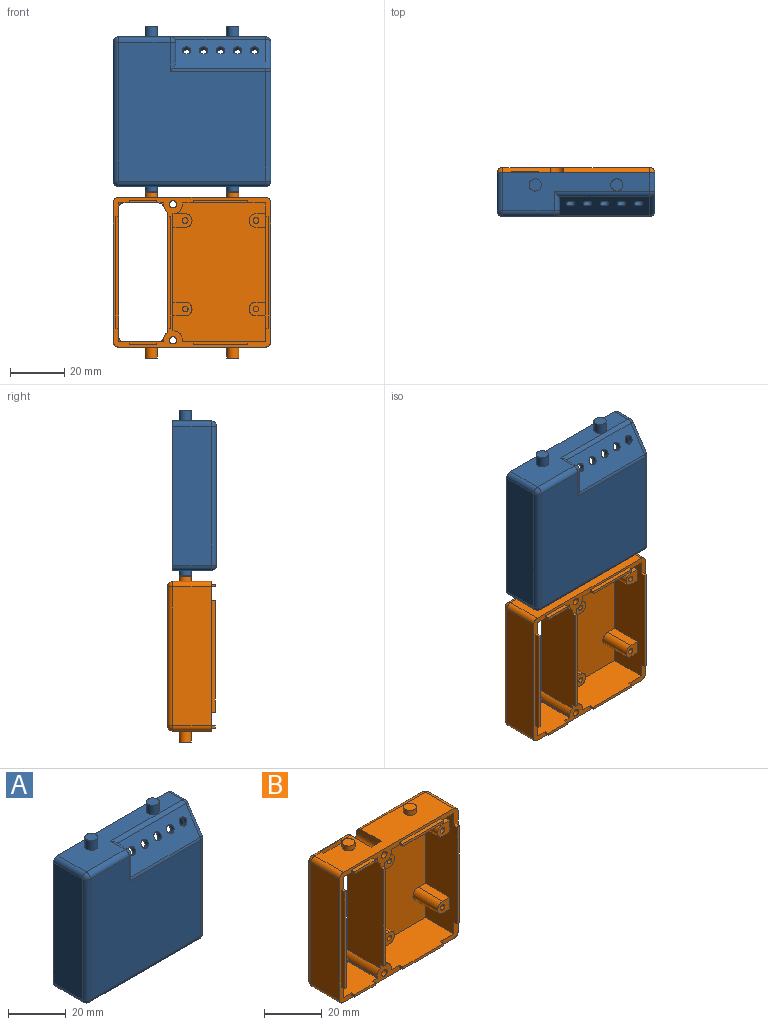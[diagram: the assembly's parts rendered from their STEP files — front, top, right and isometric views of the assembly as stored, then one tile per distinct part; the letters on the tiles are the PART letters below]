
ASSEMBLY  parts=2 mates=1
PART A: 117 faces, bbox 58x16x61 mm
  f0: plane 17x14mm, normal (0,0,1), area 216mm2, adj f2,f19,f27,f36,f97,f99,f100
  f1: plane 31x14mm, normal (0,0,1), area 392mm2, adj f2,f3,f16,f37,f105,f106,f108
  f2: plane 58x55mm, normal (0,1,0), area 343.2mm2, adj f0,f1,f3,f4,f17,f18,f20,f21
  f3: plane 51x14mm, normal (-1,0,0), area 509.9mm2, adj f1,f2,f5,f6,f7,f11,f15,f16
  f4: plane 45.53x14mm, normal (-1,0,0), area 555.4mm2, adj f2,f19,f34,f35,f82,f83,f84
  f5: plane 7.76x3.5mm, normal (0,0,1), area 27.2mm2, adj f3,f8,f15,f47
  f6: plane 8.5x3.5mm, normal (0,0,-1), area 29.8mm2, adj f3,f12,f16,f45
  f7: plane 8.5x3.5mm, normal (0,0,-1), area 29.8mm2, adj f3,f8,f16,f47
  f8: cylinder r=2.5mm len=8.5mm, axis (0,1,0), area 65.6mm2, adj f5,f7,f15,f16,f47
  f9: plane 8.5x4.5mm, normal (0,0,-1), area 38.2mm2, adj f10,f16,f39,f46
  f10: cylinder r=2.5mm len=8.5mm, axis (0,1,0), area 65.6mm2, adj f9,f15,f16,f42,f46
  f11: plane 8.5x3.5mm, normal (0,0,1), area 29.8mm2, adj f3,f12,f16,f45
  f12: cylinder r=2.5mm len=8.5mm, axis (0,1,0), area 66.8mm2, adj f6,f11,f16,f45
  f13: plane 8.5x4.5mm, normal (0,0,1), area 38.2mm2, adj f14,f16,f39,f44
  f14: cylinder r=2.5mm len=8.5mm, axis (0,1,0), area 66.8mm2, adj f13,f16,f43,f44
  f15: plane 34x10.61mm, normal (0,0.83,-0.55), area 368.4mm2, adj f3,f5,f8,f10,f16,f18,f28,f29
  f16: plane 40.39x34mm, normal (0,1,0), area 1257.6mm2, adj f1,f3,f6,f7,f8,f9,f10,f11
  f17: plane 17x14mm, normal (0,0,-1), area 216mm2, adj f2,f19,f27,f33,f102,f103,f104
  f18: plane 31x6.93mm, normal (0,0,-1), area 172.8mm2, adj f2,f3,f15,f41,f94,f95,f96
  f19: plane 51x18mm, normal (0,1,0), area 913.9mm2, adj f0,f4,f17,f27,f33,f34,f35,f36
  f20: plane 51x14mm, normal (1,0,0), area 676.5mm2, adj f2,f66,f67,f74,f75
  f21: plane 54x14mm, normal (0,0,1), area 476.7mm2, adj f2,f62,f65,f66,f69,f70,f113,f115
  f22: plane 54x51mm, normal (0,-1,0), area 2382.8mm2, adj f61,f68,f69,f75,f76,f78
  f23: plane 51x14mm, normal (-1,0,0), area 714mm2, adj f2,f60,f61,f62
  f24: plane 54x14mm, normal (0,0,-1), area 724.2mm2, adj f2,f60,f67,f68,f109,f111
  f25: plane 33.89x10.61mm, normal (0,-0.83,0.55), area 381.4mm2, adj f26,f28,f29,f30,f31,f32,f65,f70
  f26: plane 7x4.67mm, normal (1,0,0), area 16.3mm2, adj f25,f70,f76
  f27: plane 51x14mm, normal (1,0,0), area 632mm2, adj f0,f2,f17,f19,f85,f87,f88
  f28: cylinder r=1.6mm len=3.77mm, axis (0,-0.83,0.55), area 20.1mm2, adj f15,f25
  f29: cylinder r=1.6mm len=3.77mm, axis (0,-0.83,0.55), area 20.1mm2, adj f15,f25
  f30: cylinder r=1.6mm len=3.77mm, axis (0,-0.83,0.55), area 20.1mm2, adj f15,f25
  f31: cylinder r=1.6mm len=3.77mm, axis (0,-0.83,0.55), area 20.1mm2, adj f15,f25
  f32: cylinder r=1.6mm len=3.77mm, axis (0,-0.83,0.55), area 20.1mm2, adj f15,f25
  f33: plane 14x0.5mm, normal (-1,0,0), area 7mm2, adj f2,f17,f19,f34
  f34: cylinder r=3mm len=14mm, axis (0,1,0), area 35.3mm2, adj f2,f4,f19,f33
  f35: cylinder r=3mm len=14mm, axis (0,1,0), area 35.3mm2, adj f2,f4,f19,f36
  f36: plane 14x0.5mm, normal (-1,0,0), area 7mm2, adj f0,f2,f19,f35
  f37: plane 14x0.5mm, normal (1,0,0), area 7mm2, adj f1,f2,f16,f38
  f38: cylinder r=3mm len=14mm, axis (0,1,0), area 66mm2, adj f2,f16,f37,f39
  f39: plane 44x14mm, normal (1,0,0), area 514.6mm2, adj f2,f9,f13,f15,f16,f38,f40,f42
  f40: cylinder r=3mm len=9.26mm, axis (0,1,0), area 40.2mm2, adj f2,f15,f39,f41
  f41: plane 7.26x0.5mm, normal (1,0,0), area 3.5mm2, adj f2,f15,f18,f40
  f42: plane 7.76x4.5mm, normal (0,0,1), area 34.9mm2, adj f10,f15,f39,f46
  f43: plane 8.5x4.5mm, normal (0,0,-1), area 38.2mm2, adj f14,f16,f39,f44
  f44: plane 7x5mm, normal (0,1,0), area 28.9mm2, adj f13,f14,f39,f43,f49
  f45: plane 6x5mm, normal (0,1,0), area 23.9mm2, adj f3,f6,f11,f12,f51
  f46: plane 7x5mm, normal (0,1,0), area 28.9mm2, adj f9,f10,f39,f42,f53
  f47: plane 6x5mm, normal (0,1,0), area 23.9mm2, adj f3,f5,f7,f8,f55
  f48: plane 2.1x2.1mm, normal (0,1,0), area 3.5mm2, adj f49
  f49: cylinder r=1.05mm len=8.5mm, axis (0,1,0), area 56.1mm2, adj f44,f48
  f50: plane 2.1x2.1mm, normal (0,1,0), area 3.5mm2, adj f51
  f51: cylinder r=1.05mm len=8.5mm, axis (0,1,0), area 56.1mm2, adj f45,f50
  f52: plane 2.1x2.1mm, normal (0,1,0), area 3.5mm2, adj f53
  f53: cylinder r=1.05mm len=8.5mm, axis (0,1,0), area 56.1mm2, adj f46,f52
  f54: plane 2.1x2.1mm, normal (0,1,0), area 3.5mm2, adj f55
  f55: cylinder r=1.05mm len=8.5mm, axis (0,1,0), area 56.1mm2, adj f47,f54
  f56: cylinder r=1.05mm len=7mm, axis (0,1,0), area 46.2mm2, adj f2,f57
  f57: plane 2.1x2.1mm, normal (0,1,0), area 1.1mm2, adj f56,f58,f59
  f58: cylinder r=1mm len=2mm, axis (0,1,0), area 2.3mm2, adj f57,f59
  f59: plane 2x1.39mm, normal (0,0.83,-0.55), area 2.8mm2, adj f57,f58
  f60: cylinder r=2mm len=14mm, axis (0,-1,0), area 44mm2, adj f2,f23,f24,f63
  f61: cylinder r=2mm len=51mm, axis (0,0,1), area 160.2mm2, adj f22,f23,f63,f64
  f62: cylinder r=2mm len=14mm, axis (0,1,0), area 44mm2, adj f2,f21,f23,f64
  f63: sphere r=2mm, area 6.3mm2, adj f60,f61,f68
  f64: sphere r=2mm, area 6.3mm2, adj f61,f62,f69
  f65: cylinder r=2mm len=35mm, axis (-1,0,0), area 67mm2, adj f21,f25,f70,f71
  f66: cylinder r=2mm len=6.93mm, axis (0,-1,0), area 21.8mm2, adj f2,f20,f21,f71
  f67: cylinder r=2mm len=14mm, axis (0,1,0), area 44mm2, adj f2,f20,f24,f72
  f68: cylinder r=2mm len=54mm, axis (-1,0,0), area 169.6mm2, adj f22,f24,f63,f72
  f69: cylinder r=2mm len=19mm, axis (1,0,0), area 59.7mm2, adj f21,f22,f64,f73
  f70: cylinder r=2mm len=7.07mm, axis (0,1,0), area 18.1mm2, adj f21,f25,f26,f65,f73
  f71: sphere r=2mm, area 3.9mm2, adj f65,f66,f74
  f72: sphere r=2mm, area 6.3mm2, adj f67,f68,f75
  f73: sphere r=2mm, area 6.3mm2, adj f69,f70,f76
  f74: cylinder r=2mm len=11.72mm, axis (0,0.55,0.83), area 40mm2, adj f20,f25,f71,f77
  f75: cylinder r=2mm len=40.39mm, axis (0,0,-1), area 126.9mm2, adj f20,f22,f72,f77
  f76: cylinder r=2mm len=10.61mm, axis (0,0,1), area 28.2mm2, adj f22,f25,f26,f73,f78
  f77: sphere r=2mm, area 2.4mm2, adj f74,f75,f78
  f78: cylinder r=2mm len=35mm, axis (-1,0,0), area 40.5mm2, adj f22,f25,f76,f77
  f79: cylinder r=1.05mm len=14mm, axis (0,1,0), area 92.4mm2, adj f2,f80
  f80: plane 2.1x2.1mm, normal (0,1,0), area 3.5mm2, adj f79
  f81: plane 41x2mm, normal (-1,0,0), area 82mm2, adj f2,f82,f83,f84
  f82: plane 2x1.1mm, normal (0,0,1), area 2.2mm2, adj f2,f4,f81,f84
  f83: plane 2x1.1mm, normal (0,0,-1), area 2.2mm2, adj f2,f4,f81,f84
  f84: plane 41x1.1mm, normal (0,1,0), area 45.1mm2, adj f4,f81,f82,f83
  f85: plane 2x1.1mm, normal (0,0,1), area 2.2mm2, adj f2,f27,f86,f88
  f86: plane 41x2mm, normal (1,0,0), area 82mm2, adj f2,f85,f87,f88
  f87: plane 2x1.1mm, normal (0,0,-1), area 2.2mm2, adj f2,f27,f86,f88
  f88: plane 41x1.1mm, normal (0,1,0), area 45.1mm2, adj f27,f85,f86,f87
  f89: plane 41x2mm, normal (-1,0,0), area 82mm2, adj f2,f90,f91,f92
  f90: plane 2x1.1mm, normal (0,0,1), area 2.2mm2, adj f2,f3,f89,f92
  f91: plane 2x1.1mm, normal (0,0,-1), area 2.2mm2, adj f2,f3,f89,f92
  f92: plane 41x1.1mm, normal (0,1,0), area 45.1mm2, adj f3,f89,f90,f91
  f93: plane 21x2mm, normal (0,0,-1), area 42mm2, adj f2,f94,f95,f96
  f94: plane 2x1.1mm, normal (-1,0,0), area 2.2mm2, adj f2,f18,f93,f96
  f95: plane 2x1.1mm, normal (1,0,0), area 2.2mm2, adj f2,f18,f93,f96
  f96: plane 21x1.1mm, normal (0,1,0), area 23.1mm2, adj f18,f93,f94,f95
  f97: plane 2x1.1mm, normal (-1,0,0), area 2.2mm2, adj f0,f2,f98,f100
  f98: plane 11x2mm, normal (0,0,1), area 22mm2, adj f2,f97,f99,f100
  f99: plane 2x1.1mm, normal (1,0,0), area 2.2mm2, adj f0,f2,f98,f100
  f100: plane 11x1.1mm, normal (0,1,0), area 12.1mm2, adj f0,f97,f98,f99
  f101: plane 11x2mm, normal (0,0,-1), area 22mm2, adj f2,f102,f103,f104
  f102: plane 2x1.1mm, normal (-1,0,0), area 2.2mm2, adj f2,f17,f101,f104
  f103: plane 2x1.1mm, normal (1,0,0), area 2.2mm2, adj f2,f17,f101,f104
  f104: plane 11x1.1mm, normal (0,1,0), area 12.1mm2, adj f17,f101,f102,f103
  f105: plane 2x1.1mm, normal (1,0,0), area 2.2mm2, adj f1,f2,f107,f108
  f106: plane 2x1.1mm, normal (-1,0,0), area 2.2mm2, adj f1,f2,f107,f108
  f107: plane 21x2mm, normal (0,0,1), area 42mm2, adj f2,f105,f106,f108
  f108: plane 21x1.1mm, normal (0,1,0), area 23.1mm2, adj f1,f105,f106,f107
  f109: cylinder r=2.25mm len=4.5mm, axis (0,0,1), area 28.3mm2, adj f24,f110
  f110: plane 4.5x4.5mm, normal (0,0,-1), area 15.9mm2, adj f109
  f111: cylinder r=2.25mm len=4.5mm, axis (0,0,1), area 28.3mm2, adj f24,f112
  f112: plane 4.5x4.5mm, normal (0,0,-1), area 15.9mm2, adj f111
  f113: cylinder r=2.25mm len=4.5mm, axis (0,0,-1), area 56.5mm2, adj f21,f114
  f114: plane 4.5x4.5mm, normal (0,0,1), area 15.9mm2, adj f113
  f115: cylinder r=2.25mm len=4.5mm, axis (0,0,-1), area 56.5mm2, adj f21,f116
  f116: plane 4.5x4.5mm, normal (0,0,1), area 15.9mm2, adj f115
PART B: 125 faces, bbox 58x17.5x61 mm
  f0: plane 1.92x1.45mm, normal (0,-1,0), area 0.6mm2, adj f24,f41,f42,f114
  f1: plane 2x2mm, normal (0,-1,0), area 0.9mm2, adj f24,f33,f115
  f2: plane 2x2mm, normal (0,-1,0), area 0.9mm2, adj f26,f33,f116
  f3: plane 2x2mm, normal (0,1,0), area 0.9mm2, adj f61,f66,f115
  f4: plane 2x2mm, normal (0,1,0), area 0.9mm2, adj f8,f66,f116
  f5: plane 54x14mm, normal (0,0,1), area 663.2mm2, adj f7,f10,f57,f61,f62,f101,f102,f104
  f6: cylinder r=1.35mm len=4mm, axis (0,-1,0), area 33.9mm2, adj f10,f101
  f7: cylinder r=2mm len=31.5mm, axis (-1,0,0), area 99mm2, adj f5,f31,f58,f102
  f8: cylinder r=2mm len=17.5mm, axis (1,0,0), area 49.9mm2, adj f4,f26,f30,f31,f67,f98,f122,f123
  f9: cylinder r=1.35mm len=4mm, axis (0,-1,0), area 33.9mm2, adj f10,f97
  f10: plane 58x55mm, normal (0,-1,0), area 366.3mm2, adj f5,f6,f9,f22,f23,f24,f25,f26
  f11: cylinder r=2.5mm len=12mm, axis (0,-1,0), area 94.2mm2, adj f12,f21,f43,f54
  f12: plane 12x3.5mm, normal (0,0,-1), area 42mm2, adj f11,f21,f32,f54
  f13: cylinder r=2.5mm len=12mm, axis (0,-1,0), area 94.2mm2, adj f14,f21,f44,f51
  f14: plane 12x4.5mm, normal (0,0,-1), area 54mm2, adj f13,f21,f22,f51
  f15: cylinder r=2.5mm len=12mm, axis (0,-1,0), area 94.2mm2, adj f16,f17,f21,f48
  f16: plane 12x3.5mm, normal (0,0,1), area 42mm2, adj f15,f21,f32,f48
  f17: plane 12x3.5mm, normal (0,0,-1), area 42mm2, adj f15,f21,f32,f48
  f18: cylinder r=2.5mm len=12mm, axis (0,-1,0), area 94.2mm2, adj f19,f20,f21,f45
  f19: plane 12x4.5mm, normal (0,0,-1), area 54mm2, adj f18,f21,f22,f45
  f20: plane 12x4.5mm, normal (0,0,1), area 54mm2, adj f18,f21,f22,f45
  f21: plane 51x34mm, normal (0,-1,0), area 1592mm2, adj f11,f12,f13,f14,f15,f16,f17,f18
  f22: plane 43x14mm, normal (1,0,0), area 482mm2, adj f10,f14,f19,f20,f21,f35,f36,f45
  f23: plane 30.5x15.5mm, normal (0,0,-1), area 457mm2, adj f10,f21,f32,f34,f69,f71,f72
  f24: plane 17.5x16.5mm, normal (0,0,-1), area 255.4mm2, adj f0,f1,f10,f33,f42,f61,f89,f91
  f25: plane 30.5x15.5mm, normal (0,0,1), area 457mm2, adj f10,f21,f32,f37,f77,f79,f80
  f26: plane 17.5x16.5mm, normal (0,0,1), area 255.4mm2, adj f2,f8,f10,f27,f33,f38,f94,f95
  f27: plane 1.92x1.45mm, normal (0,-1,0), area 0.6mm2, adj f26,f38,f39,f113
  f28: plane 51x14mm, normal (1,0,0), area 714mm2, adj f10,f57,f59,f60
  f29: plane 51x14mm, normal (-1,0,0), area 714mm2, adj f10,f62,f66,f68
  f30: plane 54x14mm, normal (0,0,-1), area 663.2mm2, adj f8,f10,f59,f65,f68,f97,f98,f100
  f31: plane 51x39.29mm, normal (0,1,0), area 1820.1mm2, adj f7,f8,f39,f40,f41,f60,f61,f65
  f32: plane 51x15.5mm, normal (-1,0,0), area 655.5mm2, adj f10,f12,f16,f17,f21,f23,f25,f43
  f33: plane 51x17.5mm, normal (1,0,0), area 869.5mm2, adj f1,f2,f10,f24,f26,f66,f86,f87
  f34: plane 14x0.5mm, normal (1,0,0), area 7mm2, adj f10,f21,f23,f35
  f35: cylinder r=3.5mm len=14mm, axis (0,-1,0), area 77mm2, adj f10,f21,f22,f34,f44
  f36: cylinder r=3.5mm len=14mm, axis (0,-1,0), area 77mm2, adj f10,f21,f22,f37
  f37: plane 14x0.5mm, normal (1,0,0), area 7mm2, adj f10,f21,f25,f36
  f38: plane 14x0.5mm, normal (-1,0,0), area 7mm2, adj f10,f26,f27,f39
  f39: cylinder r=3.5mm len=16mm, axis (0,-1,0), area 52mm2, adj f10,f27,f31,f38,f40,f113
  f40: plane 44.26x17.5mm, normal (-1,0,0), area 769.6mm2, adj f10,f31,f39,f41,f81,f83,f84
  f41: cylinder r=3.5mm len=16mm, axis (0,-1,0), area 52mm2, adj f0,f10,f31,f40,f42,f114
  f42: plane 14x0.5mm, normal (-1,0,0), area 7mm2, adj f0,f10,f24,f41
  f43: plane 12x3.5mm, normal (0,0,1), area 42mm2, adj f11,f21,f32,f54
  f44: plane 12x4.5mm, normal (0,0,1), area 54mm2, adj f13,f21,f35,f51
  f45: plane 7x5mm, normal (0,-1,0), area 28.9mm2, adj f18,f19,f20,f22,f47
  f46: plane 2.1x2.1mm, normal (0,-1,0), area 3.5mm2, adj f47
  f47: cylinder r=1.05mm len=12mm, axis (0,-1,0), area 79.2mm2, adj f45,f46
  f48: plane 6x5mm, normal (0,-1,0), area 23.9mm2, adj f15,f16,f17,f32,f50
  f49: plane 2.1x2.1mm, normal (0,-1,0), area 3.5mm2, adj f50
  f50: cylinder r=1.05mm len=12mm, axis (0,-1,0), area 79.2mm2, adj f48,f49
  f51: plane 7x5mm, normal (0,-1,0), area 28.9mm2, adj f13,f14,f22,f44,f53
  f52: plane 2.1x2.1mm, normal (0,-1,0), area 3.5mm2, adj f53
  f53: cylinder r=1.05mm len=12mm, axis (0,-1,0), area 79.2mm2, adj f51,f52
  f54: plane 6x5mm, normal (0,-1,0), area 23.9mm2, adj f11,f12,f32,f43,f56
  f55: plane 2.1x2.1mm, normal (0,-1,0), area 3.5mm2, adj f56
  f56: cylinder r=1.05mm len=12mm, axis (0,-1,0), area 79.2mm2, adj f54,f55
  f57: cylinder r=2mm len=14mm, axis (0,-1,0), area 44mm2, adj f5,f10,f28,f58
  f58: sphere r=2mm, area 6.3mm2, adj f7,f57,f60
  f59: cylinder r=2mm len=14mm, axis (0,1,0), area 44mm2, adj f10,f28,f30,f63
  f60: cylinder r=2mm len=51mm, axis (0,0,1), area 160.2mm2, adj f28,f31,f58,f63
  f61: cylinder r=2mm len=17.5mm, axis (-1,0,0), area 49.9mm2, adj f3,f5,f24,f31,f64,f104,f117,f118
  f62: cylinder r=2mm len=14mm, axis (0,1,0), area 44mm2, adj f5,f10,f29,f64
  f63: sphere r=2mm, area 6.3mm2, adj f59,f60,f65
  f64: sphere r=2mm, area 6.3mm2, adj f61,f62,f66
  f65: cylinder r=2mm len=31.5mm, axis (1,0,0), area 99mm2, adj f30,f31,f63,f100
  f66: cylinder r=2mm len=51mm, axis (0,0,-1), area 160.2mm2, adj f3,f4,f29,f33,f64,f67
  f67: sphere r=2mm, area 6.3mm2, adj f8,f66,f68
  f68: cylinder r=2mm len=14mm, axis (0,-1,0), area 44mm2, adj f10,f29,f30,f67
  f69: plane 1.5x1mm, normal (1,0,0), area 1.5mm2, adj f10,f23,f70,f72
  f70: plane 20x1.5mm, normal (0,0,1), area 30mm2, adj f10,f69,f71,f72
  f71: plane 1.5x1mm, normal (-1,0,0), area 1.5mm2, adj f10,f23,f70,f72
  f72: plane 20x1mm, normal (0,-1,0), area 20mm2, adj f23,f69,f70,f71
  f73: plane 1.5x1mm, normal (0,0,-1), area 1.5mm2, adj f10,f32,f74,f76
  f74: plane 41x1.5mm, normal (1,0,0), area 61.5mm2, adj f10,f73,f75,f76
  f75: plane 1.5x1mm, normal (0,0,1), area 1.5mm2, adj f10,f32,f74,f76
  f76: plane 41x1mm, normal (0,-1,0), area 41mm2, adj f32,f73,f74,f75
  f77: plane 1.5x1mm, normal (-1,0,0), area 1.5mm2, adj f10,f25,f78,f80
  f78: plane 20x1.5mm, normal (0,0,-1), area 30mm2, adj f10,f77,f79,f80
  f79: plane 1.5x1mm, normal (1,0,0), area 1.5mm2, adj f10,f25,f78,f80
  f80: plane 20x1mm, normal (0,-1,0), area 20mm2, adj f25,f77,f78,f79
  f81: plane 1.5x1.1mm, normal (0,0,-1), area 1.6mm2, adj f10,f40,f82,f84
  f82: plane 41x1.5mm, normal (1,0,0), area 61.5mm2, adj f10,f81,f83,f84
  f83: plane 1.5x1.1mm, normal (0,0,1), area 1.6mm2, adj f10,f40,f82,f84
  f84: plane 41x1.1mm, normal (0,-1,0), area 45.1mm2, adj f40,f81,f82,f83
  f85: plane 41x1.5mm, normal (-1,0,0), area 61.5mm2, adj f10,f86,f87,f88
  f86: plane 1.5x1mm, normal (0,0,-1), area 1.5mm2, adj f10,f33,f85,f88
  f87: plane 1.5x1mm, normal (0,0,1), area 1.5mm2, adj f10,f33,f85,f88
  f88: plane 41x1mm, normal (0,-1,0), area 41mm2, adj f33,f85,f86,f87
  f89: plane 1.5x1mm, normal (1,0,0), area 1.5mm2, adj f10,f24,f90,f92
  f90: plane 10x1.5mm, normal (0,0,1), area 15mm2, adj f10,f89,f91,f92
  f91: plane 1.5x1mm, normal (-1,0,0), area 1.5mm2, adj f10,f24,f90,f92
  f92: plane 10x1mm, normal (0,-1,0), area 10mm2, adj f24,f89,f90,f91
  f93: plane 10x1.5mm, normal (0,0,-1), area 15mm2, adj f10,f94,f95,f96
  f94: plane 1.5x1mm, normal (1,0,0), area 1.5mm2, adj f10,f26,f93,f96
  f95: plane 1.5x1mm, normal (-1,0,0), area 1.5mm2, adj f10,f26,f93,f96
  f96: plane 10x1mm, normal (0,-1,0), area 10mm2, adj f26,f93,f94,f95
  f97: plane 5x5mm, normal (0,1,0), area 16.6mm2, adj f9,f30,f98,f99,f100
  f98: plane 12x2.5mm, normal (1,0,0), area 29.1mm2, adj f8,f30,f31,f97,f99
  f99: cylinder r=2.5mm len=12mm, axis (0,1,0), area 94.2mm2, adj f31,f97,f98,f100
  f100: plane 12x2.5mm, normal (-1,0,0), area 29.1mm2, adj f30,f31,f65,f97,f99
  f101: plane 5x5mm, normal (0,1,0), area 16.6mm2, adj f5,f6,f102,f103,f104
  f102: plane 12x2.5mm, normal (-1,0,0), area 29.1mm2, adj f5,f7,f31,f101,f103
  f103: cylinder r=2.5mm len=12mm, axis (0,1,0), area 94.2mm2, adj f31,f101,f102,f104
  f104: plane 12x2.5mm, normal (1,0,0), area 29.1mm2, adj f5,f31,f61,f101,f103
  f105: cylinder r=2.25mm len=4.5mm, axis (0,0,1), area 56.5mm2, adj f30,f106
  f106: plane 4.5x4.5mm, normal (0,0,-1), area 15.9mm2, adj f105
  f107: cylinder r=2.25mm len=4.5mm, axis (0,0,1), area 56.5mm2, adj f30,f108
  f108: plane 4.5x4.5mm, normal (0,0,-1), area 15.9mm2, adj f107
  f109: cylinder r=2.25mm len=4.5mm, axis (0,0,-1), area 28.3mm2, adj f5,f110
  f110: plane 4.5x4.5mm, normal (0,0,1), area 15.9mm2, adj f109
  f111: cylinder r=2.25mm len=4.5mm, axis (0,0,-1), area 28.3mm2, adj f5,f112
  f112: plane 4.5x4.5mm, normal (0,0,1), area 15.9mm2, adj f111
  f113: cylinder r=2mm len=2mm, axis (0,-1,0), area 5.2mm2, adj f26,f27,f31,f39
  f114: cylinder r=2mm len=2mm, axis (0,-1,0), area 5.2mm2, adj f0,f24,f31,f41
  f115: cylinder r=2mm len=2mm, axis (0,-1,0), area 6.3mm2, adj f1,f3,f24,f33
  f116: cylinder r=2mm len=2mm, axis (0,-1,0), area 6.3mm2, adj f2,f4,f26,f33
  f117: plane 2x1.6mm, normal (1,0,0), area 3.2mm2, adj f5,f24,f61,f118,f120
  f118: plane 10x1.94mm, normal (0,-1,0), area 19.4mm2, adj f24,f61,f117,f119
  f119: plane 2x1.6mm, normal (-1,0,0), area 3.2mm2, adj f5,f24,f61,f118,f120
  f120: plane 10x2mm, normal (0,1,0), area 20mm2, adj f5,f24,f117,f119
  f121: plane 10x2mm, normal (0,1,0), area 20mm2, adj f26,f30,f122,f124
  f122: plane 2x1.6mm, normal (-1,0,0), area 3.2mm2, adj f8,f26,f30,f121,f123
  f123: plane 10x1.94mm, normal (0,-1,0), area 19.4mm2, adj f8,f26,f122,f124
  f124: plane 2x1.6mm, normal (1,0,0), area 3.2mm2, adj f8,f26,f30,f121,f123
PLACE A t=(13.33,34.5,48.61)mm
PLACE B t=(13.33,20.5,-10.39)mm
MATE fastened A.f111 <-> B.f107  axis (0,0,-1) through (28.33,30,19.11)mm
